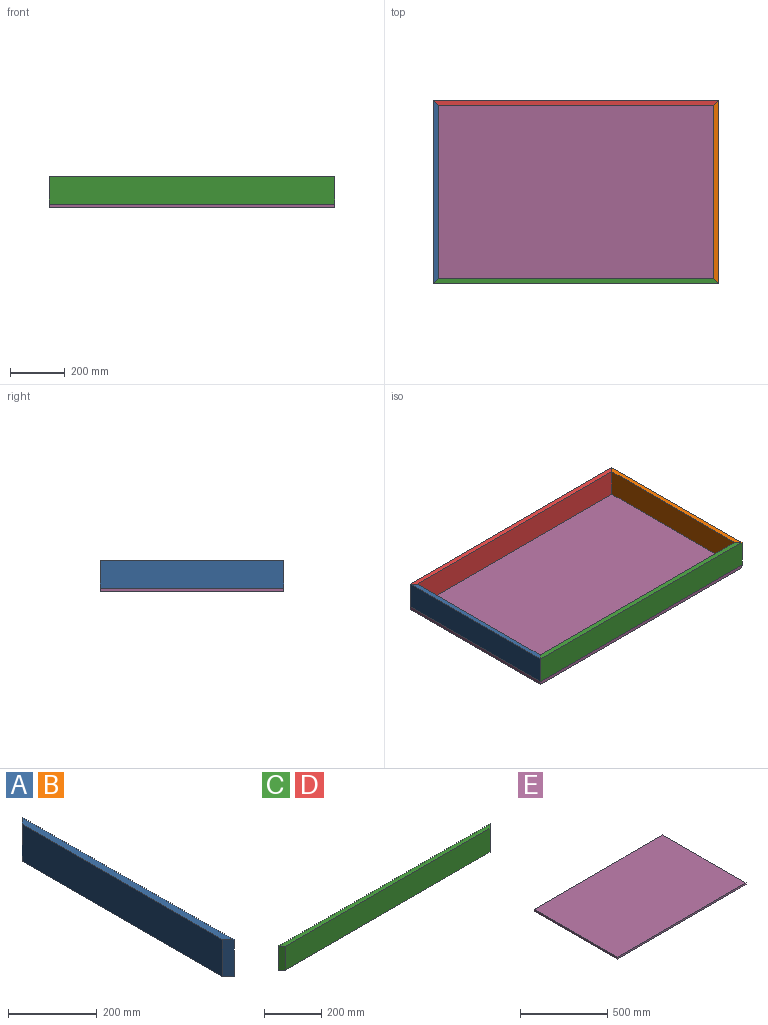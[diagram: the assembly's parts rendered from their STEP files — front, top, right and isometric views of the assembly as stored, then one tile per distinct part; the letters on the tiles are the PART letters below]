
ASSEMBLY  parts=5 mates=6
PART A: 6 faces, bbox 19.1x674.8x101.6 mm
  f0: plane 674.76x19.05mm, normal (0,0,-1), area 12491.2mm2, adj f1,f2,f3,f4
  f1: plane 101.6x19.05mm, normal (-0.71,-0.71,0), area 2737.2mm2, adj f0,f2,f4,f5
  f2: plane 674.76x101.6mm, normal (1,0,0), area 68555.3mm2, adj f0,f1,f3,f5
  f3: plane 101.6x19.05mm, normal (-0.71,0.71,0), area 2737.2mm2, adj f0,f2,f4,f5
  f4: plane 636.66x101.6mm, normal (-1,0,0), area 64684.3mm2, adj f0,f1,f3,f5
  f5: plane 674.76x19.05mm, normal (0,0,1), area 12491.2mm2, adj f1,f2,f3,f4
PART B: same geometry as A
PART C: 6 faces, bbox 1048x19.1x101.6 mm
  f0: plane 1047.96x19.05mm, normal (0,0,-1), area 19600.8mm2, adj f1,f2,f3,f4
  f1: plane 101.6x19.05mm, normal (0.71,-0.71,0), area 2737.2mm2, adj f0,f2,f4,f5
  f2: plane 1047.96x101.6mm, normal (0,1,0), area 106473.2mm2, adj f0,f1,f3,f5
  f3: plane 101.6x19.05mm, normal (-0.71,-0.71,0), area 2737.2mm2, adj f0,f2,f4,f5
  f4: plane 1009.86x101.6mm, normal (0,-1,0), area 102602.3mm2, adj f0,f1,f3,f5
  f5: plane 1047.96x19.05mm, normal (0,0,1), area 19600.8mm2, adj f1,f2,f3,f4
PART D: same geometry as C
PART E: 6 faces, bbox 1048x674.8x12.7 mm
  f0: plane 1047.96x12.7mm, normal (0,1,0), area 13309.2mm2, adj f1,f3,f4,f5
  f1: plane 674.76x12.7mm, normal (-1,0,0), area 8569.4mm2, adj f0,f2,f4,f5
  f2: plane 1047.96x12.7mm, normal (0,-1,0), area 13309.2mm2, adj f1,f3,f4,f5
  f3: plane 674.76x12.7mm, normal (1,0,0), area 8569.4mm2, adj f0,f2,f4,f5
  f4: plane 1047.96x674.76mm, normal (0,0,-1), area 707121.2mm2, adj f0,f1,f2,f3
  f5: plane 1047.96x674.76mm, normal (0,0,1), area 707121.2mm2, adj f0,f1,f2,f3
PLACE A rot(axis=(0,0,1),180deg) t=(-467.17,429.07,0)mm
PLACE B t=(-467.17,429.07,0)mm
PLACE C rot(axis=(0,0,1),180deg) t=(-467.17,429.07,0)mm
PLACE D rot(axis=(-0.52,0.03,-0.86),0deg) t=(-467.17,429.07,0)mm
PLACE E rot(axis=(0.66,-0.04,-0.75),0deg) t=(-467.17,429.07,0)mm
MATE planar E.f5 <-> C.f0  axis (0,0,1) through (-467.17,429.07,622.3)mm
MATE fastened B.f3 <-> D.f1  axis (-0.71,0.71,0) through (47.29,756.92,673.1)mm
MATE fastened D.f3 <-> A.f1  axis (-0.71,-0.71,0) through (-981.63,756.92,673.1)mm
MATE planar E.f3 <-> B.f2  axis (1,0,0) through (56.81,429.07,615.95)mm
MATE planar D.f2 <-> E.f0  axis (0,1,0) through (-467.17,766.45,673.1)mm
MATE fastened C.f3 <-> B.f1  axis (0.71,0.71,0) through (47.29,101.22,673.1)mm
